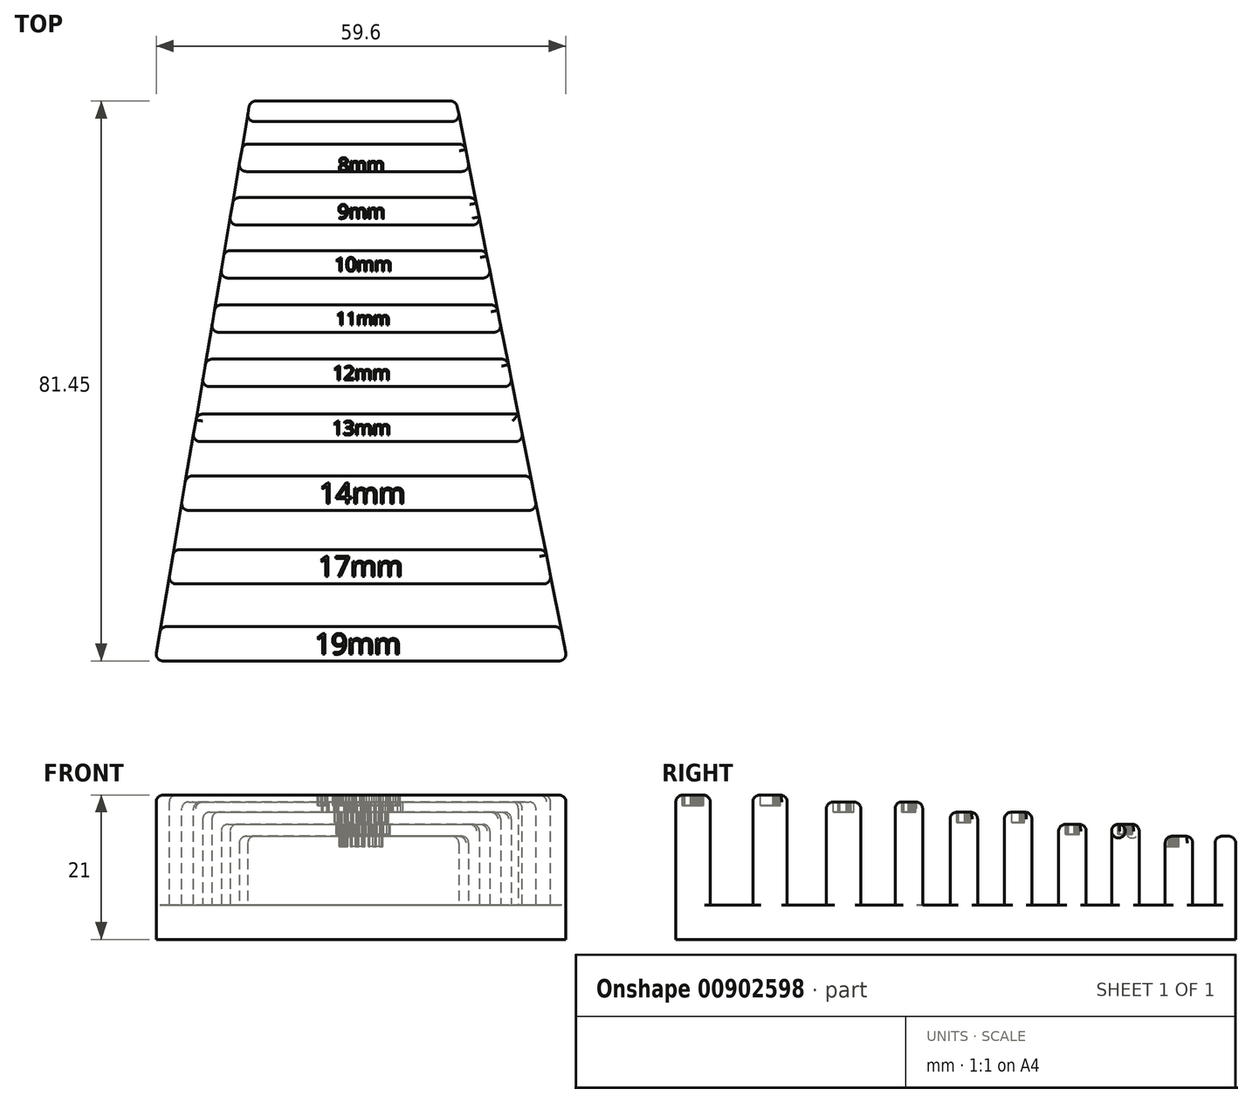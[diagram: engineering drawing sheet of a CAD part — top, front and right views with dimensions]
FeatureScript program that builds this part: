
annotation { "Feature Type Name" : "Feature", "Feature Type Description" : "" }
export const myFeature = defineFeature(function(context is Context, id is Id, definition is map)
    precondition{}
    {
        {
            var Q0;
            Q0=qCreatedBy(makeId("Top.planeOp"),FACE);
            var sketch = newSketch(context, id + "F0", { "sketchPlane" : qUnion([Q0])});
            skLineSegment(sketch, "E0.top", {"start": v(-30, -26.46) * mm, "end": v(30, -26.46) * mm});
            skLineSegment(sketch, "E1", {"start": v(-30, -26.46) * mm, "end": v(-16.18, 55) * mm});
            skLineSegment(sketch, "E2", {"start": v(-16.18, 55) * mm, "end": v(13.82, 55) * mm});
            skLineSegment(sketch, "E3", {"start": v(13.82, 55) * mm, "end": v(30, -26.46) * mm});
            skSolve(sketch);
        }
        {
            var Q0;
            Q0 = qSketchRegion(id + "F0", true);
            extrude(context, id + "F1", {"entities" : qUnion([Q0]), "depth" : 5 * mm, "offsetDistance" : 25 * mm});
        }
        {
            var Q0;
            Q0=makeQuery(id+"F1.opExtrude","CAP_FACE",FACE,{"disambiguationData":[OSD([sQuery(id+"F0.wireOp",EDGE,"E0.top"),sQuery(id+"F0.wireOp",EDGE,"E1"),sQuery(id+"F0.wireOp",EDGE,"E2"),sQuery(id+"F0.wireOp",EDGE,"E3")])],"isStart":false});
            var sketch = newSketch(context, id + "F2", { "sketchPlane" : qUnion([Q0])});
            skLineSegment(sketch, "E4", {"start": v(-16.18, 55) * mm, "end": v(13.82, 55) * mm});
            skLineSegment(sketch, "E5", {"start": v(13.82, 55) * mm, "end": v(14.42, 52) * mm});
            skLineSegment(sketch, "E6", {"start": v(14.42, 52) * mm, "end": v(-16.69, 52) * mm});
            skLineSegment(sketch, "E7", {"start": v(-16.69, 52) * mm, "end": v(-16.18, 55) * mm});
            skLineSegment(sketch, "E8", {"start": v(-17.24, 48.74) * mm, "end": v(15.06, 48.74) * mm});
            skLineSegment(sketch, "E9", {"start": v(15.06, 48.74) * mm, "end": v(15.86, 44.74) * mm});
            skLineSegment(sketch, "E10", {"start": v(15.86, 44.74) * mm, "end": v(-17.92, 44.74) * mm});
            skLineSegment(sketch, "E11", {"start": v(-17.92, 44.74) * mm, "end": v(-17.24, 48.74) * mm});
            skLineSegment(sketch, "E12", {"start": v(-18.56, 40.94) * mm, "end": v(16.61, 40.94) * mm});
            skLineSegment(sketch, "E13", {"start": v(16.61, 40.94) * mm, "end": v(17.4, 36.94) * mm});
            skLineSegment(sketch, "E14", {"start": v(17.4, 36.94) * mm, "end": v(-19.24, 36.94) * mm});
            skLineSegment(sketch, "E15", {"start": v(-19.24, 36.94) * mm, "end": v(-18.56, 40.94) * mm});
            skLineSegment(sketch, "E16", {"start": v(-19.87, 33.24) * mm, "end": v(18.14, 33.24) * mm});
            skLineSegment(sketch, "E17", {"start": v(18.14, 33.24) * mm, "end": v(18.94, 29.24) * mm});
            skLineSegment(sketch, "E18", {"start": v(18.94, 29.24) * mm, "end": v(-20.55, 29.24) * mm});
            skLineSegment(sketch, "E19", {"start": v(-20.55, 29.24) * mm, "end": v(-19.87, 33.24) * mm});
            skLineSegment(sketch, "E20", {"start": v(-21.21, 25.34) * mm, "end": v(19.71, 25.34) * mm});
            skLineSegment(sketch, "E21", {"start": v(19.71, 25.34) * mm, "end": v(20.5, 21.34) * mm});
            skLineSegment(sketch, "E22", {"start": v(20.5, 21.34) * mm, "end": v(-21.89, 21.34) * mm});
            skLineSegment(sketch, "E23", {"start": v(-21.89, 21.34) * mm, "end": v(-21.21, 25.34) * mm});
            skLineSegment(sketch, "E24", {"start": v(-22.55, 17.44) * mm, "end": v(21.28, 17.44) * mm});
            skLineSegment(sketch, "E25", {"start": v(21.28, 17.44) * mm, "end": v(22.07, 13.44) * mm});
            skLineSegment(sketch, "E26", {"start": v(22.07, 13.44) * mm, "end": v(-23.23, 13.44) * mm});
            skLineSegment(sketch, "E27", {"start": v(-23.23, 13.44) * mm, "end": v(-22.55, 17.44) * mm});
            skLineSegment(sketch, "E28", {"start": v(-23.9, 9.44) * mm, "end": v(22.87, 9.44) * mm});
            skLineSegment(sketch, "E29", {"start": v(-24.59, 5.44) * mm, "end": v(23.66, 5.44) * mm});
            skLineSegment(sketch, "E30", {"start": v(24.66, 0.44) * mm, "end": v(-25.44, 0.44) * mm});
            skLineSegment(sketch, "E31", {"start": v(-26.28, -4.56) * mm, "end": v(25.65, -4.56) * mm});
            skLineSegment(sketch, "E32", {"start": v(26.78, -10.26) * mm, "end": v(-27.25, -10.26) * mm});
            skLineSegment(sketch, "E33", {"start": v(-28.1, -15.26) * mm, "end": v(27.78, -15.26) * mm});
            skLineSegment(sketch, "E34", {"start": v(29, -21.46) * mm, "end": v(-29.15, -21.46) * mm});
            skLineSegment(sketch, "E35", {"start": v(22.87, 9.44) * mm, "end": v(23.66, 5.44) * mm});
            skLineSegment(sketch, "E36", {"start": v(-24.59, 5.44) * mm, "end": v(-23.9, 9.44) * mm});
            skLineSegment(sketch, "E37", {"start": v(24.66, 0.44) * mm, "end": v(25.65, -4.56) * mm});
            skLineSegment(sketch, "E38", {"start": v(26.78, -10.26) * mm, "end": v(27.78, -15.26) * mm});
            skLineSegment(sketch, "E39", {"start": v(-28.1, -15.26) * mm, "end": v(-27.25, -10.26) * mm});
            skLineSegment(sketch, "E40", {"start": v(-26.28, -4.56) * mm, "end": v(-25.44, 0.44) * mm});
            skLineSegment(sketch, "E41", {"start": v(29, -21.46) * mm, "end": v(30, -26.46) * mm});
            skLineSegment(sketch, "E42", {"start": v(30, -26.46) * mm, "end": v(-30, -26.46) * mm});
            skLineSegment(sketch, "E43", {"start": v(-30, -26.46) * mm, "end": v(-29.15, -21.46) * mm});
            skSolve(sketch);
        }
        {
            var Q0;
            Q0 = qSketchRegion(id + "F2", true);
            extrude(context, id + "F3", {"entities" : qUnion([Q0]), "operationType" : NewBodyOperationType.ADD, "depth" : 10 * mm, "offsetDistance" : 25 * mm});
        }
        {
            var Q0;
            Q0=makeQuery(id+"F3.opExtrude","CAP_FACE",FACE,{"disambiguationData":[OSD([sQuery(id+"F2.wireOp",EDGE,"E34"),sQuery(id+"F2.wireOp",EDGE,"E41"),sQuery(id+"F2.wireOp",EDGE,"E42"),sQuery(id+"F2.wireOp",EDGE,"E43")])],"isStart":false});
            extrude(context, id + "F4", {"entities" : qUnion([Q0]), "operationType" : NewBodyOperationType.ADD, "depth" : 6 * mm, "offsetDistance" : 25 * mm});
        }
        {
            var Q0;
            Q0=makeQuery(id+"F3.opExtrude","CAP_FACE",FACE,{"disambiguationData":[OSD([sQuery(id+"F2.wireOp",EDGE,"E32"),sQuery(id+"F2.wireOp",EDGE,"E33"),sQuery(id+"F2.wireOp",EDGE,"E38"),sQuery(id+"F2.wireOp",EDGE,"E39")])],"isStart":false});
            extrude(context, id + "F5", {"entities" : qUnion([Q0]), "operationType" : NewBodyOperationType.ADD, "depth" : 6 * mm, "offsetDistance" : 25 * mm});
        }
        {
            var Q0;
            Q0=makeQuery(id+"F3.opExtrude","CAP_FACE",FACE,{"disambiguationData":[OSD([sQuery(id+"F2.wireOp",EDGE,"E30"),sQuery(id+"F2.wireOp",EDGE,"E31"),sQuery(id+"F2.wireOp",EDGE,"E37"),sQuery(id+"F2.wireOp",EDGE,"E40")])],"isStart":false});
            var Q1;
            Q1=makeQuery(id+"F3.opExtrude","CAP_FACE",FACE,{"disambiguationData":[OSD([sQuery(id+"F2.wireOp",EDGE,"E28"),sQuery(id+"F2.wireOp",EDGE,"E29"),sQuery(id+"F2.wireOp",EDGE,"E35"),sQuery(id+"F2.wireOp",EDGE,"E36")])],"isStart":false});
            extrude(context, id + "F6", {"entities" : qUnion([Q0, Q1]), "operationType" : NewBodyOperationType.ADD, "depth" : 5 * mm, "offsetDistance" : 25 * mm});
        }
        {
            var Q0;
            Q0=makeQuery(id+"F3.opExtrude","CAP_FACE",FACE,{"disambiguationData":[OSD([sQuery(id+"F2.wireOp",EDGE,"E20"),sQuery(id+"F2.wireOp",EDGE,"E21"),sQuery(id+"F2.wireOp",EDGE,"E22"),sQuery(id+"F2.wireOp",EDGE,"E23")])],"isStart":false});
            var Q1;
            Q1=makeQuery(id+"F3.opExtrude","CAP_FACE",FACE,{"disambiguationData":[OSD([sQuery(id+"F2.wireOp",EDGE,"E24"),sQuery(id+"F2.wireOp",EDGE,"E25"),sQuery(id+"F2.wireOp",EDGE,"E26"),sQuery(id+"F2.wireOp",EDGE,"E27")])],"isStart":false});
            extrude(context, id + "F7", {"entities" : qUnion([Q0, Q1]), "operationType" : NewBodyOperationType.ADD, "depth" : 3.5 * mm, "offsetDistance" : 25 * mm});
        }
        {
            var Q0;
            Q0=makeQuery(id+"F3.opExtrude","CAP_FACE",FACE,{"disambiguationData":[OSD([sQuery(id+"F2.wireOp",EDGE,"E16"),sQuery(id+"F2.wireOp",EDGE,"E17"),sQuery(id+"F2.wireOp",EDGE,"E18"),sQuery(id+"F2.wireOp",EDGE,"E19")])],"isStart":false});
            var Q1;
            Q1=makeQuery(id+"F3.opExtrude","CAP_FACE",FACE,{"disambiguationData":[OSD([sQuery(id+"F2.wireOp",EDGE,"E12"),sQuery(id+"F2.wireOp",EDGE,"E13"),sQuery(id+"F2.wireOp",EDGE,"E14"),sQuery(id+"F2.wireOp",EDGE,"E15")])],"isStart":false});
            extrude(context, id + "F8", {"entities" : qUnion([Q0, Q1]), "operationType" : NewBodyOperationType.ADD, "depth" : 1.75 * mm, "offsetDistance" : 25 * mm});
        }
        {
            var Q0;
            Q0=makeQuery(id+"F3.opExtrude","CAP_EDGE",EDGE,{"disambiguationData":[OSD([sQuery(id+"F2.wireOp",EDGE,"E4")])],"isStart":false});
            var Q1;
            Q1=makeQuery(id+"F3.opExtrude","CAP_EDGE",EDGE,{"disambiguationData":[OSD([sQuery(id+"F2.wireOp",EDGE,"E8")])],"isStart":false});
            var Q2;
            Q2=makeQuery(id+"F3.opExtrude","CAP_EDGE",EDGE,{"disambiguationData":[OSD([sQuery(id+"F2.wireOp",EDGE,"E6")])],"isStart":false});
            var Q3;
            Q3=makeQuery(id+"F3.opExtrude","CAP_EDGE",EDGE,{"disambiguationData":[OSD([sQuery(id+"F2.wireOp",EDGE,"E7")])],"isStart":false});
            var Q4;
            Q4=makeQuery(id+"F3.opExtrude","CAP_EDGE",EDGE,{"disambiguationData":[OSD([sQuery(id+"F2.wireOp",EDGE,"E11")])],"isStart":false});
            var Q5;
            Q5=makeQuery(id+"F3.opExtrude","CAP_EDGE",EDGE,{"disambiguationData":[OSD([sQuery(id+"F2.wireOp",EDGE,"E10")])],"isStart":false});
            var Q6;
            Q6=makeQuery(id+"F8.opExtrude","CAP_EDGE",EDGE,{"disambiguationData":[OSD([sQuery(id+"F2.wireOp",EDGE,"E15")])],"isStart":false});
            var Q7;
            Q7=makeQuery(id+"F8.opExtrude","CAP_EDGE",EDGE,{"disambiguationData":[OSD([sQuery(id+"F2.wireOp",EDGE,"E12")])],"isStart":false});
            var Q8;
            Q8=makeQuery(id+"F8.opExtrude","CAP_EDGE",EDGE,{"disambiguationData":[OSD([sQuery(id+"F2.wireOp",EDGE,"E14")])],"isStart":false});
            var Q9;
            {var subQ0=sQuery(id+"F2.wireOp",EDGE,"E15");var subQ1=sQuery(id+"F2.wireOp",EDGE,"E14");var subQ2=sQuery(id+"F0.wireOp",EDGE,"E1");Q9=makeQuery(id+"F8.boolean.opBoolean","MERGE",EDGE,{"derivedFrom":[makeQuery(id+"F3.opExtrude","SWEPT_EDGE",EDGE,{"disambiguationData":[OSD([subQ2,subQ1,subQ0])]}),makeQuery(id+"F8.opExtrude","SWEPT_EDGE",EDGE,{"disambiguationData":[OSD([subQ2,subQ1,subQ0])]})]});}
            var Q10;
            {var subQ0=sQuery(id+"F2.wireOp",EDGE,"E15");var subQ1=sQuery(id+"F2.wireOp",EDGE,"E12");var subQ2=sQuery(id+"F0.wireOp",EDGE,"E1");Q10=makeQuery(id+"F8.boolean.opBoolean","MERGE",EDGE,{"derivedFrom":[makeQuery(id+"F3.opExtrude","SWEPT_EDGE",EDGE,{"disambiguationData":[OSD([subQ2,subQ1,subQ0])]}),makeQuery(id+"F8.opExtrude","SWEPT_EDGE",EDGE,{"disambiguationData":[OSD([subQ2,subQ1,subQ0])]})]});}
            var Q11;
            Q11=makeQuery(id+"F3.opExtrude","SWEPT_EDGE",EDGE,{"disambiguationData":[OSD([sQuery(id+"F0.wireOp",EDGE,"E1"),sQuery(id+"F2.wireOp",EDGE,"E6"),sQuery(id+"F2.wireOp",EDGE,"E7")])]});
            var Q12;
            Q12=makeQuery(id+"F3.boolean.opBoolean","MERGE",EDGE,{"derivedFrom":[makeQuery(id+"F1.opExtrude","SWEPT_EDGE",EDGE,{"disambiguationData":[OSD([sQuery(id+"F0.wireOp",EDGE,"E1"),sQuery(id+"F0.wireOp",EDGE,"E2")])]}),makeQuery(id+"F3.opExtrude","SWEPT_EDGE",EDGE,{"disambiguationData":[OSD([sQuery(id+"F2.wireOp",EDGE,"E4"),sQuery(id+"F2.wireOp",EDGE,"E7")])]})]});
            var Q13;
            Q13=makeQuery(id+"F3.opExtrude","SWEPT_EDGE",EDGE,{"disambiguationData":[OSD([sQuery(id+"F0.wireOp",EDGE,"E1"),sQuery(id+"F2.wireOp",EDGE,"E8"),sQuery(id+"F2.wireOp",EDGE,"E11")])]});
            var Q14;
            Q14=makeQuery(id+"F3.opExtrude","SWEPT_EDGE",EDGE,{"disambiguationData":[OSD([sQuery(id+"F0.wireOp",EDGE,"E1"),sQuery(id+"F2.wireOp",EDGE,"E10"),sQuery(id+"F2.wireOp",EDGE,"E11")])]});
            var Q15;
            {var subQ0=sQuery(id+"F2.wireOp",EDGE,"E19");var subQ1=sQuery(id+"F2.wireOp",EDGE,"E16");var subQ2=sQuery(id+"F0.wireOp",EDGE,"E1");Q15=makeQuery(id+"F8.boolean.opBoolean","MERGE",EDGE,{"derivedFrom":[makeQuery(id+"F3.opExtrude","SWEPT_EDGE",EDGE,{"disambiguationData":[OSD([subQ2,subQ1,subQ0])]}),makeQuery(id+"F8.opExtrude","SWEPT_EDGE",EDGE,{"disambiguationData":[OSD([subQ2,subQ1,subQ0])]})]});}
            var Q16;
            Q16=makeQuery(id+"F8.opExtrude","CAP_EDGE",EDGE,{"disambiguationData":[OSD([sQuery(id+"F2.wireOp",EDGE,"E16")])],"isStart":false});
            var Q17;
            Q17=makeQuery(id+"F8.opExtrude","CAP_EDGE",EDGE,{"disambiguationData":[OSD([sQuery(id+"F2.wireOp",EDGE,"E18")])],"isStart":false});
            var Q18;
            {var subQ0=sQuery(id+"F2.wireOp",EDGE,"E19");var subQ1=sQuery(id+"F2.wireOp",EDGE,"E18");var subQ2=sQuery(id+"F0.wireOp",EDGE,"E1");Q18=makeQuery(id+"F8.boolean.opBoolean","MERGE",EDGE,{"derivedFrom":[makeQuery(id+"F3.opExtrude","SWEPT_EDGE",EDGE,{"disambiguationData":[OSD([subQ2,subQ1,subQ0])]}),makeQuery(id+"F8.opExtrude","SWEPT_EDGE",EDGE,{"disambiguationData":[OSD([subQ2,subQ1,subQ0])]})]});}
            var Q19;
            Q19=makeQuery(id+"F8.opExtrude","CAP_EDGE",EDGE,{"disambiguationData":[OSD([sQuery(id+"F2.wireOp",EDGE,"E19")])],"isStart":false});
            var Q20;
            Q20=makeQuery(id+"F7.opExtrude","CAP_EDGE",EDGE,{"disambiguationData":[OSD([sQuery(id+"F2.wireOp",EDGE,"E23")])],"isStart":false});
            var Q21;
            {var subQ0=sQuery(id+"F2.wireOp",EDGE,"E23");var subQ1=sQuery(id+"F2.wireOp",EDGE,"E20");var subQ2=sQuery(id+"F0.wireOp",EDGE,"E1");Q21=makeQuery(id+"F7.boolean.opBoolean","MERGE",EDGE,{"derivedFrom":[makeQuery(id+"F3.opExtrude","SWEPT_EDGE",EDGE,{"disambiguationData":[OSD([subQ2,subQ1,subQ0])]}),makeQuery(id+"F7.opExtrude","SWEPT_EDGE",EDGE,{"disambiguationData":[OSD([subQ2,subQ1,subQ0])]})]});}
            var Q22;
            Q22=makeQuery(id+"F7.opExtrude","CAP_EDGE",EDGE,{"disambiguationData":[OSD([sQuery(id+"F2.wireOp",EDGE,"E20")])],"isStart":false});
            var Q23;
            Q23=makeQuery(id+"F7.opExtrude","CAP_EDGE",EDGE,{"disambiguationData":[OSD([sQuery(id+"F2.wireOp",EDGE,"E22")])],"isStart":false});
            var Q24;
            {var subQ0=sQuery(id+"F2.wireOp",EDGE,"E23");var subQ1=sQuery(id+"F2.wireOp",EDGE,"E22");var subQ2=sQuery(id+"F0.wireOp",EDGE,"E1");Q24=makeQuery(id+"F7.boolean.opBoolean","MERGE",EDGE,{"derivedFrom":[makeQuery(id+"F3.opExtrude","SWEPT_EDGE",EDGE,{"disambiguationData":[OSD([subQ2,subQ1,subQ0])]}),makeQuery(id+"F7.opExtrude","SWEPT_EDGE",EDGE,{"disambiguationData":[OSD([subQ2,subQ1,subQ0])]})]});}
            var Q25;
            {var subQ0=sQuery(id+"F2.wireOp",EDGE,"E27");var subQ1=sQuery(id+"F2.wireOp",EDGE,"E24");var subQ2=sQuery(id+"F0.wireOp",EDGE,"E1");Q25=makeQuery(id+"F7.boolean.opBoolean","MERGE",EDGE,{"derivedFrom":[makeQuery(id+"F3.opExtrude","SWEPT_EDGE",EDGE,{"disambiguationData":[OSD([subQ2,subQ1,subQ0])]}),makeQuery(id+"F7.opExtrude","SWEPT_EDGE",EDGE,{"disambiguationData":[OSD([subQ2,subQ1,subQ0])]})]});}
            var Q26;
            Q26=makeQuery(id+"F7.opExtrude","CAP_EDGE",EDGE,{"disambiguationData":[OSD([sQuery(id+"F2.wireOp",EDGE,"E24")])],"isStart":false});
            var Q27;
            Q27=makeQuery(id+"F7.opExtrude","CAP_EDGE",EDGE,{"disambiguationData":[OSD([sQuery(id+"F2.wireOp",EDGE,"E27")])],"isStart":false});
            var Q28;
            Q28=makeQuery(id+"F7.opExtrude","CAP_EDGE",EDGE,{"disambiguationData":[OSD([sQuery(id+"F2.wireOp",EDGE,"E26")])],"isStart":false});
            var Q29;
            {var subQ0=sQuery(id+"F2.wireOp",EDGE,"E27");var subQ1=sQuery(id+"F2.wireOp",EDGE,"E26");var subQ2=sQuery(id+"F0.wireOp",EDGE,"E1");Q29=makeQuery(id+"F7.boolean.opBoolean","MERGE",EDGE,{"derivedFrom":[makeQuery(id+"F3.opExtrude","SWEPT_EDGE",EDGE,{"disambiguationData":[OSD([subQ2,subQ1,subQ0])]}),makeQuery(id+"F7.opExtrude","SWEPT_EDGE",EDGE,{"disambiguationData":[OSD([subQ2,subQ1,subQ0])]})]});}
            var Q30;
            {var subQ0=sQuery(id+"F2.wireOp",EDGE,"E36");var subQ1=sQuery(id+"F2.wireOp",EDGE,"E28");var subQ2=sQuery(id+"F0.wireOp",EDGE,"E1");Q30=makeQuery(id+"F6.boolean.opBoolean","MERGE",EDGE,{"derivedFrom":[makeQuery(id+"F3.opExtrude","SWEPT_EDGE",EDGE,{"disambiguationData":[OSD([subQ2,subQ1,subQ0])]}),makeQuery(id+"F6.opExtrude","SWEPT_EDGE",EDGE,{"disambiguationData":[OSD([subQ2,subQ1,subQ0])]})]});}
            var Q31;
            Q31=makeQuery(id+"F6.opExtrude","CAP_EDGE",EDGE,{"disambiguationData":[OSD([sQuery(id+"F2.wireOp",EDGE,"E28")])],"isStart":false});
            var Q32;
            Q32=makeQuery(id+"F6.opExtrude","CAP_EDGE",EDGE,{"disambiguationData":[OSD([sQuery(id+"F2.wireOp",EDGE,"E36")])],"isStart":false});
            var Q33;
            Q33=makeQuery(id+"F6.opExtrude","CAP_EDGE",EDGE,{"disambiguationData":[OSD([sQuery(id+"F2.wireOp",EDGE,"E29")])],"isStart":false});
            var Q34;
            {var subQ0=sQuery(id+"F2.wireOp",EDGE,"E36");var subQ1=sQuery(id+"F2.wireOp",EDGE,"E29");var subQ2=sQuery(id+"F0.wireOp",EDGE,"E1");Q34=makeQuery(id+"F6.boolean.opBoolean","MERGE",EDGE,{"derivedFrom":[makeQuery(id+"F3.opExtrude","SWEPT_EDGE",EDGE,{"disambiguationData":[OSD([subQ2,subQ1,subQ0])]}),makeQuery(id+"F6.opExtrude","SWEPT_EDGE",EDGE,{"disambiguationData":[OSD([subQ2,subQ1,subQ0])]})]});}
            var Q35;
            {var subQ0=sQuery(id+"F2.wireOp",EDGE,"E40");var subQ1=sQuery(id+"F2.wireOp",EDGE,"E30");var subQ2=sQuery(id+"F0.wireOp",EDGE,"E1");Q35=makeQuery(id+"F6.boolean.opBoolean","MERGE",EDGE,{"derivedFrom":[makeQuery(id+"F3.opExtrude","SWEPT_EDGE",EDGE,{"disambiguationData":[OSD([subQ2,subQ1,subQ0])]}),makeQuery(id+"F6.opExtrude","SWEPT_EDGE",EDGE,{"disambiguationData":[OSD([subQ2,subQ1,subQ0])]})]});}
            var Q36;
            Q36=makeQuery(id+"F6.opExtrude","CAP_EDGE",EDGE,{"disambiguationData":[OSD([sQuery(id+"F2.wireOp",EDGE,"E30")])],"isStart":false});
            var Q37;
            Q37=makeQuery(id+"F6.opExtrude","CAP_EDGE",EDGE,{"disambiguationData":[OSD([sQuery(id+"F2.wireOp",EDGE,"E40")])],"isStart":false});
            var Q38;
            Q38=makeQuery(id+"F6.opExtrude","CAP_EDGE",EDGE,{"disambiguationData":[OSD([sQuery(id+"F2.wireOp",EDGE,"E31")])],"isStart":false});
            var Q39;
            {var subQ0=sQuery(id+"F2.wireOp",EDGE,"E40");var subQ1=sQuery(id+"F2.wireOp",EDGE,"E31");var subQ2=sQuery(id+"F0.wireOp",EDGE,"E1");Q39=makeQuery(id+"F6.boolean.opBoolean","MERGE",EDGE,{"derivedFrom":[makeQuery(id+"F3.opExtrude","SWEPT_EDGE",EDGE,{"disambiguationData":[OSD([subQ2,subQ1,subQ0])]}),makeQuery(id+"F6.opExtrude","SWEPT_EDGE",EDGE,{"disambiguationData":[OSD([subQ2,subQ1,subQ0])]})]});}
            var Q40;
            {var subQ0=sQuery(id+"F2.wireOp",EDGE,"E39");var subQ1=sQuery(id+"F2.wireOp",EDGE,"E32");var subQ2=sQuery(id+"F0.wireOp",EDGE,"E1");Q40=makeQuery(id+"F5.boolean.opBoolean","MERGE",EDGE,{"derivedFrom":[makeQuery(id+"F3.opExtrude","SWEPT_EDGE",EDGE,{"disambiguationData":[OSD([subQ2,subQ1,subQ0])]}),makeQuery(id+"F5.opExtrude","SWEPT_EDGE",EDGE,{"disambiguationData":[OSD([subQ2,subQ1,subQ0])]})]});}
            var Q41;
            Q41=makeQuery(id+"F5.opExtrude","CAP_EDGE",EDGE,{"disambiguationData":[OSD([sQuery(id+"F2.wireOp",EDGE,"E32")])],"isStart":false});
            var Q42;
            Q42=makeQuery(id+"F5.opExtrude","CAP_EDGE",EDGE,{"disambiguationData":[OSD([sQuery(id+"F2.wireOp",EDGE,"E39")])],"isStart":false});
            var Q43;
            Q43=makeQuery(id+"F5.opExtrude","CAP_EDGE",EDGE,{"disambiguationData":[OSD([sQuery(id+"F2.wireOp",EDGE,"E33")])],"isStart":false});
            var Q44;
            {var subQ0=sQuery(id+"F2.wireOp",EDGE,"E39");var subQ1=sQuery(id+"F2.wireOp",EDGE,"E33");var subQ2=sQuery(id+"F0.wireOp",EDGE,"E1");Q44=makeQuery(id+"F5.boolean.opBoolean","MERGE",EDGE,{"derivedFrom":[makeQuery(id+"F3.opExtrude","SWEPT_EDGE",EDGE,{"disambiguationData":[OSD([subQ2,subQ1,subQ0])]}),makeQuery(id+"F5.opExtrude","SWEPT_EDGE",EDGE,{"disambiguationData":[OSD([subQ2,subQ1,subQ0])]})]});}
            var Q45;
            Q45=makeQuery(id+"F4.opExtrude","CAP_EDGE",EDGE,{"disambiguationData":[OSD([sQuery(id+"F2.wireOp",EDGE,"E34")])],"isStart":false});
            var Q46;
            {var subQ0=sQuery(id+"F2.wireOp",EDGE,"E43");var subQ1=sQuery(id+"F2.wireOp",EDGE,"E34");var subQ2=sQuery(id+"F0.wireOp",EDGE,"E1");Q46=makeQuery(id+"F4.boolean.opBoolean","MERGE",EDGE,{"derivedFrom":[makeQuery(id+"F3.opExtrude","SWEPT_EDGE",EDGE,{"disambiguationData":[OSD([subQ2,subQ1,subQ0])]}),makeQuery(id+"F4.opExtrude","SWEPT_EDGE",EDGE,{"disambiguationData":[OSD([subQ2,subQ1,subQ0])]})]});}
            var Q47;
            Q47=makeQuery(id+"F4.opExtrude","CAP_EDGE",EDGE,{"disambiguationData":[OSD([sQuery(id+"F2.wireOp",EDGE,"E43")])],"isStart":false});
            var Q48;
            Q48=makeQuery(id+"F4.opExtrude","CAP_EDGE",EDGE,{"disambiguationData":[OSD([sQuery(id+"F2.wireOp",EDGE,"E42")])],"isStart":false});
            var Q49;
            {var subQ0=sQuery(id+"F2.wireOp",EDGE,"E43");var subQ1=sQuery(id+"F2.wireOp",EDGE,"E42");Q49=makeQuery(id+"F4.boolean.opBoolean","MERGE",EDGE,{"derivedFrom":[makeQuery(id+"F3.boolean.opBoolean","MERGE",EDGE,{"derivedFrom":[makeQuery(id+"F1.opExtrude","SWEPT_EDGE",EDGE,{"disambiguationData":[OSD([sQuery(id+"F0.wireOp",EDGE,"E0.top"),sQuery(id+"F0.wireOp",EDGE,"E1")])]}),makeQuery(id+"F3.opExtrude","SWEPT_EDGE",EDGE,{"disambiguationData":[OSD([subQ1,subQ0])]})]}),makeQuery(id+"F4.opExtrude","SWEPT_EDGE",EDGE,{"disambiguationData":[OSD([subQ1,subQ0])]})]});}
            var Q50;
            Q50=makeQuery(id+"F4.opExtrude","CAP_EDGE",EDGE,{"disambiguationData":[OSD([sQuery(id+"F2.wireOp",EDGE,"E41")])],"isStart":false});
            var Q51;
            {var subQ0=sQuery(id+"F2.wireOp",EDGE,"E38");var subQ1=sQuery(id+"F2.wireOp",EDGE,"E33");var subQ2=sQuery(id+"F0.wireOp",EDGE,"E3");Q51=makeQuery(id+"F5.boolean.opBoolean","MERGE",EDGE,{"derivedFrom":[makeQuery(id+"F3.opExtrude","SWEPT_EDGE",EDGE,{"disambiguationData":[OSD([subQ2,subQ1,subQ0])]}),makeQuery(id+"F5.opExtrude","SWEPT_EDGE",EDGE,{"disambiguationData":[OSD([subQ2,subQ1,subQ0])]})]});}
            var Q52;
            Q52=makeQuery(id+"F5.opExtrude","CAP_EDGE",EDGE,{"disambiguationData":[OSD([sQuery(id+"F2.wireOp",EDGE,"E38")])],"isStart":false});
            var Q53;
            {var subQ0=sQuery(id+"F2.wireOp",EDGE,"E38");var subQ1=sQuery(id+"F2.wireOp",EDGE,"E32");var subQ2=sQuery(id+"F0.wireOp",EDGE,"E3");Q53=makeQuery(id+"F5.boolean.opBoolean","MERGE",EDGE,{"derivedFrom":[makeQuery(id+"F3.opExtrude","SWEPT_EDGE",EDGE,{"disambiguationData":[OSD([subQ2,subQ1,subQ0])]}),makeQuery(id+"F5.opExtrude","SWEPT_EDGE",EDGE,{"disambiguationData":[OSD([subQ2,subQ1,subQ0])]})]});}
            var Q54;
            {var subQ0=sQuery(id+"F2.wireOp",EDGE,"E37");var subQ1=sQuery(id+"F2.wireOp",EDGE,"E31");var subQ2=sQuery(id+"F0.wireOp",EDGE,"E3");Q54=makeQuery(id+"F6.boolean.opBoolean","MERGE",EDGE,{"derivedFrom":[makeQuery(id+"F3.opExtrude","SWEPT_EDGE",EDGE,{"disambiguationData":[OSD([subQ2,subQ1,subQ0])]}),makeQuery(id+"F6.opExtrude","SWEPT_EDGE",EDGE,{"disambiguationData":[OSD([subQ2,subQ1,subQ0])]})]});}
            var Q55;
            Q55=makeQuery(id+"F6.opExtrude","CAP_EDGE",EDGE,{"disambiguationData":[OSD([sQuery(id+"F2.wireOp",EDGE,"E37")])],"isStart":false});
            var Q56;
            {var subQ0=sQuery(id+"F2.wireOp",EDGE,"E37");var subQ1=sQuery(id+"F2.wireOp",EDGE,"E30");var subQ2=sQuery(id+"F0.wireOp",EDGE,"E3");Q56=makeQuery(id+"F6.boolean.opBoolean","MERGE",EDGE,{"derivedFrom":[makeQuery(id+"F3.opExtrude","SWEPT_EDGE",EDGE,{"disambiguationData":[OSD([subQ2,subQ1,subQ0])]}),makeQuery(id+"F6.opExtrude","SWEPT_EDGE",EDGE,{"disambiguationData":[OSD([subQ2,subQ1,subQ0])]})]});}
            var Q57;
            {var subQ0=sQuery(id+"F2.wireOp",EDGE,"E35");var subQ1=sQuery(id+"F2.wireOp",EDGE,"E29");var subQ2=sQuery(id+"F0.wireOp",EDGE,"E3");Q57=makeQuery(id+"F6.boolean.opBoolean","MERGE",EDGE,{"derivedFrom":[makeQuery(id+"F3.opExtrude","SWEPT_EDGE",EDGE,{"disambiguationData":[OSD([subQ2,subQ1,subQ0])]}),makeQuery(id+"F6.opExtrude","SWEPT_EDGE",EDGE,{"disambiguationData":[OSD([subQ2,subQ1,subQ0])]})]});}
            var Q58;
            Q58=makeQuery(id+"F6.opExtrude","CAP_EDGE",EDGE,{"disambiguationData":[OSD([sQuery(id+"F2.wireOp",EDGE,"E35")])],"isStart":false});
            var Q59;
            {var subQ0=sQuery(id+"F2.wireOp",EDGE,"E26");var subQ1=sQuery(id+"F2.wireOp",EDGE,"E25");var subQ2=sQuery(id+"F0.wireOp",EDGE,"E3");Q59=makeQuery(id+"F7.boolean.opBoolean","MERGE",EDGE,{"derivedFrom":[makeQuery(id+"F3.opExtrude","SWEPT_EDGE",EDGE,{"disambiguationData":[OSD([subQ2,subQ1,subQ0])]}),makeQuery(id+"F7.opExtrude","SWEPT_EDGE",EDGE,{"disambiguationData":[OSD([subQ2,subQ1,subQ0])]})]});}
            var Q60;
            Q60=makeQuery(id+"F7.opExtrude","CAP_EDGE",EDGE,{"disambiguationData":[OSD([sQuery(id+"F2.wireOp",EDGE,"E25")])],"isStart":false});
            var Q61;
            {var subQ0=sQuery(id+"F2.wireOp",EDGE,"E25");var subQ1=sQuery(id+"F2.wireOp",EDGE,"E24");var subQ2=sQuery(id+"F0.wireOp",EDGE,"E3");Q61=makeQuery(id+"F7.boolean.opBoolean","MERGE",EDGE,{"derivedFrom":[makeQuery(id+"F3.opExtrude","SWEPT_EDGE",EDGE,{"disambiguationData":[OSD([subQ2,subQ1,subQ0])]}),makeQuery(id+"F7.opExtrude","SWEPT_EDGE",EDGE,{"disambiguationData":[OSD([subQ2,subQ1,subQ0])]})]});}
            var Q62;
            {var subQ0=sQuery(id+"F2.wireOp",EDGE,"E22");var subQ1=sQuery(id+"F2.wireOp",EDGE,"E21");var subQ2=sQuery(id+"F0.wireOp",EDGE,"E3");Q62=makeQuery(id+"F7.boolean.opBoolean","MERGE",EDGE,{"derivedFrom":[makeQuery(id+"F3.opExtrude","SWEPT_EDGE",EDGE,{"disambiguationData":[OSD([subQ2,subQ1,subQ0])]}),makeQuery(id+"F7.opExtrude","SWEPT_EDGE",EDGE,{"disambiguationData":[OSD([subQ2,subQ1,subQ0])]})]});}
            var Q63;
            Q63=makeQuery(id+"F7.opExtrude","CAP_EDGE",EDGE,{"disambiguationData":[OSD([sQuery(id+"F2.wireOp",EDGE,"E21")])],"isStart":false});
            var Q64;
            {var subQ0=sQuery(id+"F2.wireOp",EDGE,"E18");var subQ1=sQuery(id+"F2.wireOp",EDGE,"E17");var subQ2=sQuery(id+"F0.wireOp",EDGE,"E3");Q64=makeQuery(id+"F8.boolean.opBoolean","MERGE",EDGE,{"derivedFrom":[makeQuery(id+"F3.opExtrude","SWEPT_EDGE",EDGE,{"disambiguationData":[OSD([subQ2,subQ1,subQ0])]}),makeQuery(id+"F8.opExtrude","SWEPT_EDGE",EDGE,{"disambiguationData":[OSD([subQ2,subQ1,subQ0])]})]});}
            var Q65;
            Q65=makeQuery(id+"F8.opExtrude","CAP_EDGE",EDGE,{"disambiguationData":[OSD([sQuery(id+"F2.wireOp",EDGE,"E17")])],"isStart":false});
            var Q66;
            {var subQ0=sQuery(id+"F2.wireOp",EDGE,"E17");var subQ1=sQuery(id+"F2.wireOp",EDGE,"E16");var subQ2=sQuery(id+"F0.wireOp",EDGE,"E3");Q66=makeQuery(id+"F8.boolean.opBoolean","MERGE",EDGE,{"derivedFrom":[makeQuery(id+"F3.opExtrude","SWEPT_EDGE",EDGE,{"disambiguationData":[OSD([subQ2,subQ1,subQ0])]}),makeQuery(id+"F8.opExtrude","SWEPT_EDGE",EDGE,{"disambiguationData":[OSD([subQ2,subQ1,subQ0])]})]});}
            var Q67;
            {var subQ0=sQuery(id+"F2.wireOp",EDGE,"E14");var subQ1=sQuery(id+"F2.wireOp",EDGE,"E13");var subQ2=sQuery(id+"F0.wireOp",EDGE,"E3");Q67=makeQuery(id+"F8.boolean.opBoolean","MERGE",EDGE,{"derivedFrom":[makeQuery(id+"F3.opExtrude","SWEPT_EDGE",EDGE,{"disambiguationData":[OSD([subQ2,subQ1,subQ0])]}),makeQuery(id+"F8.opExtrude","SWEPT_EDGE",EDGE,{"disambiguationData":[OSD([subQ2,subQ1,subQ0])]})]});}
            var Q68;
            Q68=makeQuery(id+"F8.opExtrude","CAP_EDGE",EDGE,{"disambiguationData":[OSD([sQuery(id+"F2.wireOp",EDGE,"E13")])],"isStart":false});
            var Q69;
            {var subQ0=sQuery(id+"F2.wireOp",EDGE,"E13");var subQ1=sQuery(id+"F2.wireOp",EDGE,"E12");var subQ2=sQuery(id+"F0.wireOp",EDGE,"E3");Q69=makeQuery(id+"F8.boolean.opBoolean","MERGE",EDGE,{"derivedFrom":[makeQuery(id+"F3.opExtrude","SWEPT_EDGE",EDGE,{"disambiguationData":[OSD([subQ2,subQ1,subQ0])]}),makeQuery(id+"F8.opExtrude","SWEPT_EDGE",EDGE,{"disambiguationData":[OSD([subQ2,subQ1,subQ0])]})]});}
            var Q70;
            Q70=makeQuery(id+"F3.opExtrude","SWEPT_EDGE",EDGE,{"disambiguationData":[OSD([sQuery(id+"F0.wireOp",EDGE,"E3"),sQuery(id+"F2.wireOp",EDGE,"E9"),sQuery(id+"F2.wireOp",EDGE,"E10")])]});
            var Q71;
            Q71=makeQuery(id+"F3.opExtrude","CAP_EDGE",EDGE,{"disambiguationData":[OSD([sQuery(id+"F2.wireOp",EDGE,"E9")])],"isStart":false});
            var Q72;
            Q72=makeQuery(id+"F3.opExtrude","SWEPT_EDGE",EDGE,{"disambiguationData":[OSD([sQuery(id+"F0.wireOp",EDGE,"E3"),sQuery(id+"F2.wireOp",EDGE,"E8"),sQuery(id+"F2.wireOp",EDGE,"E9")])]});
            var Q73;
            Q73=makeQuery(id+"F3.opExtrude","SWEPT_EDGE",EDGE,{"disambiguationData":[OSD([sQuery(id+"F0.wireOp",EDGE,"E3"),sQuery(id+"F2.wireOp",EDGE,"E5"),sQuery(id+"F2.wireOp",EDGE,"E6")])]});
            var Q74;
            Q74=makeQuery(id+"F3.boolean.opBoolean","MERGE",EDGE,{"derivedFrom":[makeQuery(id+"F1.opExtrude","SWEPT_EDGE",EDGE,{"disambiguationData":[OSD([sQuery(id+"F0.wireOp",EDGE,"E2"),sQuery(id+"F0.wireOp",EDGE,"E3")])]}),makeQuery(id+"F3.opExtrude","SWEPT_EDGE",EDGE,{"disambiguationData":[OSD([sQuery(id+"F2.wireOp",EDGE,"E4"),sQuery(id+"F2.wireOp",EDGE,"E5")])]})]});
            var Q75;
            Q75=makeQuery(id+"F3.opExtrude","CAP_EDGE",EDGE,{"disambiguationData":[OSD([sQuery(id+"F2.wireOp",EDGE,"E5")])],"isStart":false});
            var Q76;
            {var subQ0=sQuery(id+"F2.wireOp",EDGE,"E41");var subQ1=sQuery(id+"F2.wireOp",EDGE,"E34");var subQ2=sQuery(id+"F0.wireOp",EDGE,"E3");Q76=makeQuery(id+"F4.boolean.opBoolean","MERGE",EDGE,{"derivedFrom":[makeQuery(id+"F3.opExtrude","SWEPT_EDGE",EDGE,{"disambiguationData":[OSD([subQ2,subQ1,subQ0])]}),makeQuery(id+"F4.opExtrude","SWEPT_EDGE",EDGE,{"disambiguationData":[OSD([subQ2,subQ1,subQ0])]})]});}
            var Q77;
            {var subQ0=sQuery(id+"F2.wireOp",EDGE,"E42");var subQ1=sQuery(id+"F2.wireOp",EDGE,"E41");Q77=makeQuery(id+"F4.boolean.opBoolean","MERGE",EDGE,{"derivedFrom":[makeQuery(id+"F3.boolean.opBoolean","MERGE",EDGE,{"derivedFrom":[makeQuery(id+"F1.opExtrude","SWEPT_EDGE",EDGE,{"disambiguationData":[OSD([sQuery(id+"F0.wireOp",EDGE,"E0.top"),sQuery(id+"F0.wireOp",EDGE,"E3")])]}),makeQuery(id+"F3.opExtrude","SWEPT_EDGE",EDGE,{"disambiguationData":[OSD([subQ1,subQ0])]})]}),makeQuery(id+"F4.opExtrude","SWEPT_EDGE",EDGE,{"disambiguationData":[OSD([subQ1,subQ0])]})]});}
            var Q78;
            {var subQ0=sQuery(id+"F2.wireOp",EDGE,"E21");var subQ1=sQuery(id+"F2.wireOp",EDGE,"E20");var subQ2=sQuery(id+"F0.wireOp",EDGE,"E3");Q78=makeQuery(id+"F7.boolean.opBoolean","MERGE",EDGE,{"derivedFrom":[makeQuery(id+"F3.opExtrude","SWEPT_EDGE",EDGE,{"disambiguationData":[OSD([subQ2,subQ1,subQ0])]}),makeQuery(id+"F7.opExtrude","SWEPT_EDGE",EDGE,{"disambiguationData":[OSD([subQ2,subQ1,subQ0])]})]});}
            fillet(context, id + "F9", {"entities" : qUnion([Q0, Q1, Q2, Q3, Q4, Q5, Q6, Q7, Q8, Q9, Q10, Q11, Q12, Q13, Q14, Q15, Q16, Q17, Q18, Q19, Q20, Q21, Q22, Q23, Q24, Q25, Q26, Q27, Q28, Q29, Q30, Q31, Q32, Q33, Q34, Q35, Q36, Q37, Q38, Q39, Q40, Q41, Q42, Q43, Q44, Q45, Q46, Q47, Q48, Q49, Q50, Q51, Q52, Q53, Q54, Q55, Q56, Q57, Q58, Q59, Q60, Q61, Q62, Q63, Q64, Q65, Q66, Q67, Q68, Q69, Q70, Q71, Q72, Q73, Q74, Q75, Q76, Q77, Q78]), "radius" : 1 * mm, "tangentPropagation" : true, "allowEdgeOverflow" : false});
        }
        {
            var Q0;
            Q0=makeQuery(id+"F5.opExtrude","CAP_FACE",FACE,{"disambiguationData":[OSD([sQuery(id+"F2.wireOp",EDGE,"E32"),sQuery(id+"F2.wireOp",EDGE,"E33"),sQuery(id+"F2.wireOp",EDGE,"E38"),sQuery(id+"F2.wireOp",EDGE,"E39")])],"isStart":false});
            var sketch = newSketch(context, id + "F10", { "sketchPlane" : qUnion([Q0])});
            skText(sketch, "E44", { "text": "19mm", "fontName": "OpenSans-Regular.ttf"});
            skText(sketch, "E45", { "text": "17mm", "fontName": "OpenSans-Regular.ttf"});
            const initialGuessF10  = {"E44": [-0.00676, -0.02546, 1, 0, 0.003], "E45": [-0.00625, -0.01416, 1, 0, 0.00295]};
            skSetInitialGuess(sketch, initialGuessF10);
            skSolve(sketch);
        }
        {
            var Q0;
            Q0 = qSketchRegion(id + "F10", true);
            extrude(context, id + "F11", {"entities" : qUnion([Q0]), "operationType" : NewBodyOperationType.REMOVE, "oppositeDirection" : true, "depth" : 1.5 * mm, "offsetDistance" : 25 * mm});
        }
        {
            var Q0;
            Q0=makeQuery(id+"F6.opExtrude","CAP_FACE",FACE,{"disambiguationData":[OSD([sQuery(id+"F2.wireOp",EDGE,"E30"),sQuery(id+"F2.wireOp",EDGE,"E31"),sQuery(id+"F2.wireOp",EDGE,"E37"),sQuery(id+"F2.wireOp",EDGE,"E40")])],"isStart":false});
            var sketch = newSketch(context, id + "F12", { "sketchPlane" : qUnion([Q0])});
            skText(sketch, "E46", { "text": "14mm", "fontName": "OpenSans-Regular.ttf"});
            skText(sketch, "E47", { "text": "13mm", "fontName": "OpenSans-Regular.ttf"});
            const initialGuessF12  = {"E46": [-0.0061, -0.00356, 1, 0, 0.003], "E47": [-0.00422, 0.00642, 1, 0, 0.00204]};
            skSetInitialGuess(sketch, initialGuessF12);
            skSolve(sketch);
        }
        {
            var Q0;
            Q0 = qSketchRegion(id + "F12", true);
            extrude(context, id + "F13", {"entities" : qUnion([Q0]), "operationType" : NewBodyOperationType.REMOVE, "oppositeDirection" : true, "depth" : 1.5 * mm, "offsetDistance" : 25 * mm});
        }
        {
            var Q0;
            Q0=makeQuery(id+"F7.opExtrude","CAP_FACE",FACE,{"disambiguationData":[OSD([sQuery(id+"F2.wireOp",EDGE,"E24"),sQuery(id+"F2.wireOp",EDGE,"E25"),sQuery(id+"F2.wireOp",EDGE,"E26"),sQuery(id+"F2.wireOp",EDGE,"E27")])],"isStart":false});
            var sketch = newSketch(context, id + "F14", { "sketchPlane" : qUnion([Q0])});
            skText(sketch, "E48", { "text": "12mm", "fontName": "OpenSans-Regular.ttf"});
            skText(sketch, "E49", { "text": "11mm", "fontName": "OpenSans-Regular.ttf"});
            const initialGuessF14  = {"E48": [-0.00412, 0.01444, 1, 0, 0.002], "E49": [-0.00367, 0.02241, 1, 0, 0.00188]};
            skSetInitialGuess(sketch, initialGuessF14);
            skSolve(sketch);
        }
        {
            var Q0;
            Q0 = qSketchRegion(id + "F14", true);
            extrude(context, id + "F15", {"entities" : qUnion([Q0]), "operationType" : NewBodyOperationType.REMOVE, "oppositeDirection" : true, "depth" : 1.5 * mm, "offsetDistance" : 25 * mm});
        }
        {
            var Q0;
            Q0=makeQuery(id+"F8.opExtrude","CAP_FACE",FACE,{"disambiguationData":[OSD([sQuery(id+"F2.wireOp",EDGE,"E16"),sQuery(id+"F2.wireOp",EDGE,"E17"),sQuery(id+"F2.wireOp",EDGE,"E18"),sQuery(id+"F2.wireOp",EDGE,"E19")])],"isStart":false});
            var sketch = newSketch(context, id + "F16", { "sketchPlane" : qUnion([Q0])});
            skText(sketch, "E50", { "text": "10mm", "fontName": "OpenSans-Regular.ttf"});
            skText(sketch, "E51", { "text": "9mm", "fontName": "OpenSans-Regular.ttf"});
            const initialGuessF16  = {"E50": [-0.00387, 0.03024, 1, 0, 0.002], "E51": [-0.00342, 0.03791, 1, 0, 0.00204]};
            skSetInitialGuess(sketch, initialGuessF16);
            skSolve(sketch);
        }
        {
            var Q0;
            Q0 = qSketchRegion(id + "F16", true);
            extrude(context, id + "F17", {"entities" : qUnion([Q0]), "operationType" : NewBodyOperationType.REMOVE, "oppositeDirection" : true, "depth" : 1.5 * mm, "offsetDistance" : 25 * mm});
        }
        {
            var Q0;
            Q0=makeQuery(id+"F3.opExtrude","CAP_FACE",FACE,{"disambiguationData":[OSD([sQuery(id+"F2.wireOp",EDGE,"E8"),sQuery(id+"F2.wireOp",EDGE,"E9"),sQuery(id+"F2.wireOp",EDGE,"E10"),sQuery(id+"F2.wireOp",EDGE,"E11")])],"isStart":false});
            var sketch = newSketch(context, id + "F18", { "sketchPlane" : qUnion([Q0])});
            skText(sketch, "E52", { "text": "8mm", "fontName": "OpenSans-Regular.ttf"});
            const initialGuessF18  = {"E52": [-0.00336, 0.04474, 1, 0, 0.002]};
            skSetInitialGuess(sketch, initialGuessF18);
            skSolve(sketch);
        }
        {
            var Q0;
            Q0 = qSketchRegion(id + "F18", true);
            extrude(context, id + "F19", {"entities" : qUnion([Q0]), "operationType" : NewBodyOperationType.REMOVE, "oppositeDirection" : true, "depth" : 1.5 * mm, "offsetDistance" : 25 * mm});
        }
    });
